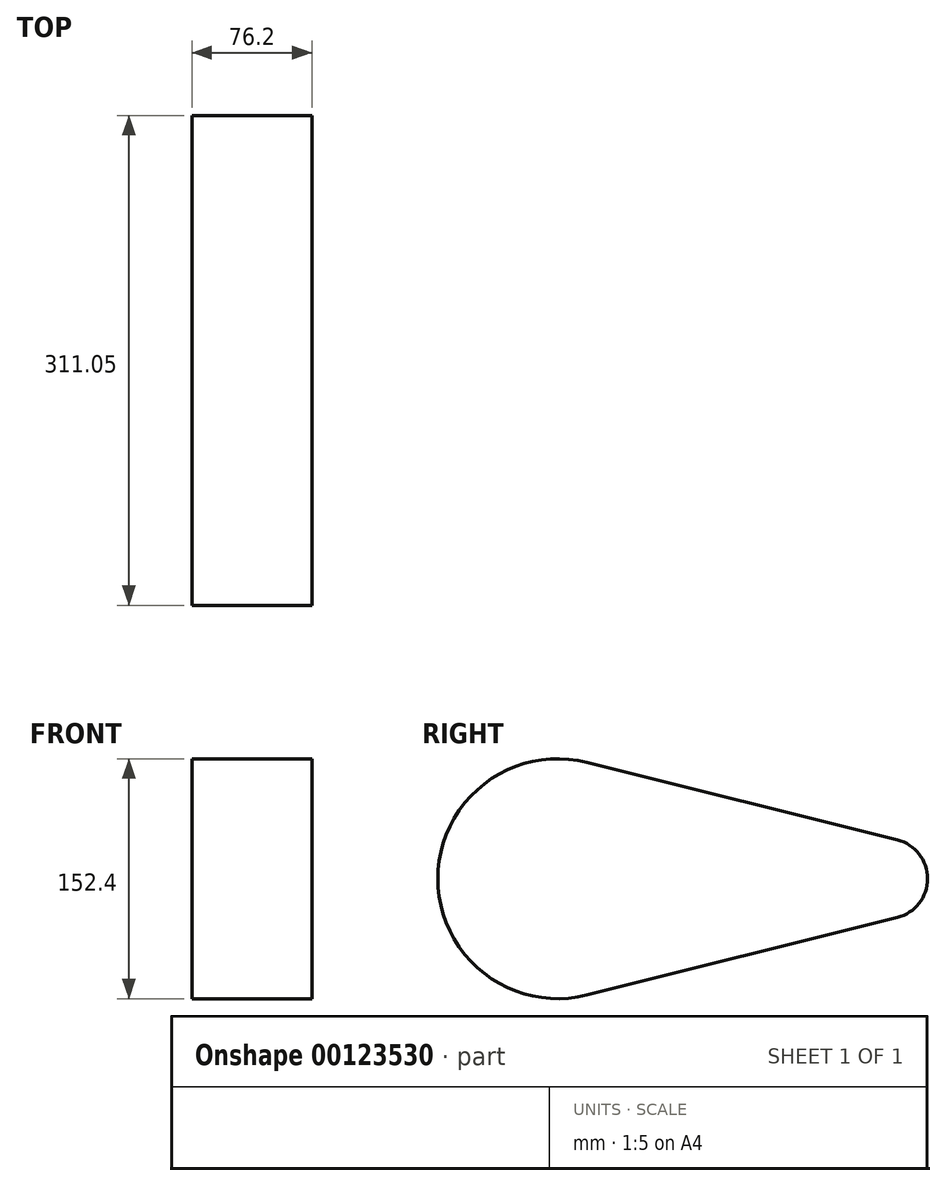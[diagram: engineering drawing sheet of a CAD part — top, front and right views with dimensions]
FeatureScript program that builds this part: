
annotation { "Feature Type Name" : "Feature", "Feature Type Description" : "" }
export const myFeature = defineFeature(function(context is Context, id is Id, definition is map)
    precondition{}
    {
        {
            var Q0;
            Q0=qCreatedBy(makeId("Right.planeOp"),FACE);
            var sketch = newSketch(context, id + "F0", { "sketchPlane" : qUnion([Q0])});
            skCircle(sketch, "E0", {"center": v(0, 0) * mm, "radius": 76.2 * mm});
            skCircle(sketch, "E1", {"center": v(209.45, 0) * mm, "radius": 25.4 * mm});
            skLineSegment(sketch, "E2", {"start": v(18.48, 73.92) * mm, "end": v(215.61, 24.64) * mm});
            skLineSegment(sketch, "E3", {"start": v(18.48, -73.92) * mm, "end": v(215.61, -24.64) * mm});
            skSolve(sketch);
        }
        {
            var Q0;
            {var subQ0=sQuery(id+"F0.wireOp",EDGE,"E0");var subQ1=makeQuery(id+"F0.imprint","INTERSECT",VERTEX,{"derivedFrom":[subQ0,sQuery(id+"F0.wireOp",EDGE,"E2")]});Q0=makeQuery(id+"F0.imprint","IMPRINT",FACE,{"disambiguationData":[TD([[makeQuery(id+"F0.imprint","IMPRINT",EDGE,{"disambiguationData":[TD([[subQ1,-1.0]])],"derivedFrom":subQ0}),1.0]])]});}
            var Q1;
            {var subQ0=sQuery(id+"F0.wireOp",EDGE,"E2");Q1=makeQuery(id+"F0.imprint","IMPRINT",FACE,{"disambiguationData":[TD([[makeQuery(id+"F0.imprint","IMPRINT",EDGE,{"derivedFrom":subQ0}),-1.0]])]});}
            var Q2;
            {var subQ0=sQuery(id+"F0.wireOp",EDGE,"E1");var subQ1=makeQuery(id+"F0.imprint","INTERSECT",VERTEX,{"derivedFrom":[subQ0,sQuery(id+"F0.wireOp",EDGE,"E2")]});Q2=makeQuery(id+"F0.imprint","IMPRINT",FACE,{"disambiguationData":[TD([[makeQuery(id+"F0.imprint","IMPRINT",EDGE,{"disambiguationData":[TD([[subQ1,-1.0]])],"derivedFrom":subQ0}),1.0]])]});}
            extrude(context, id + "F1", {"entities" : qUnion([Q0, Q1, Q2]), "depth" : 76.2 * mm});
        }
    });
